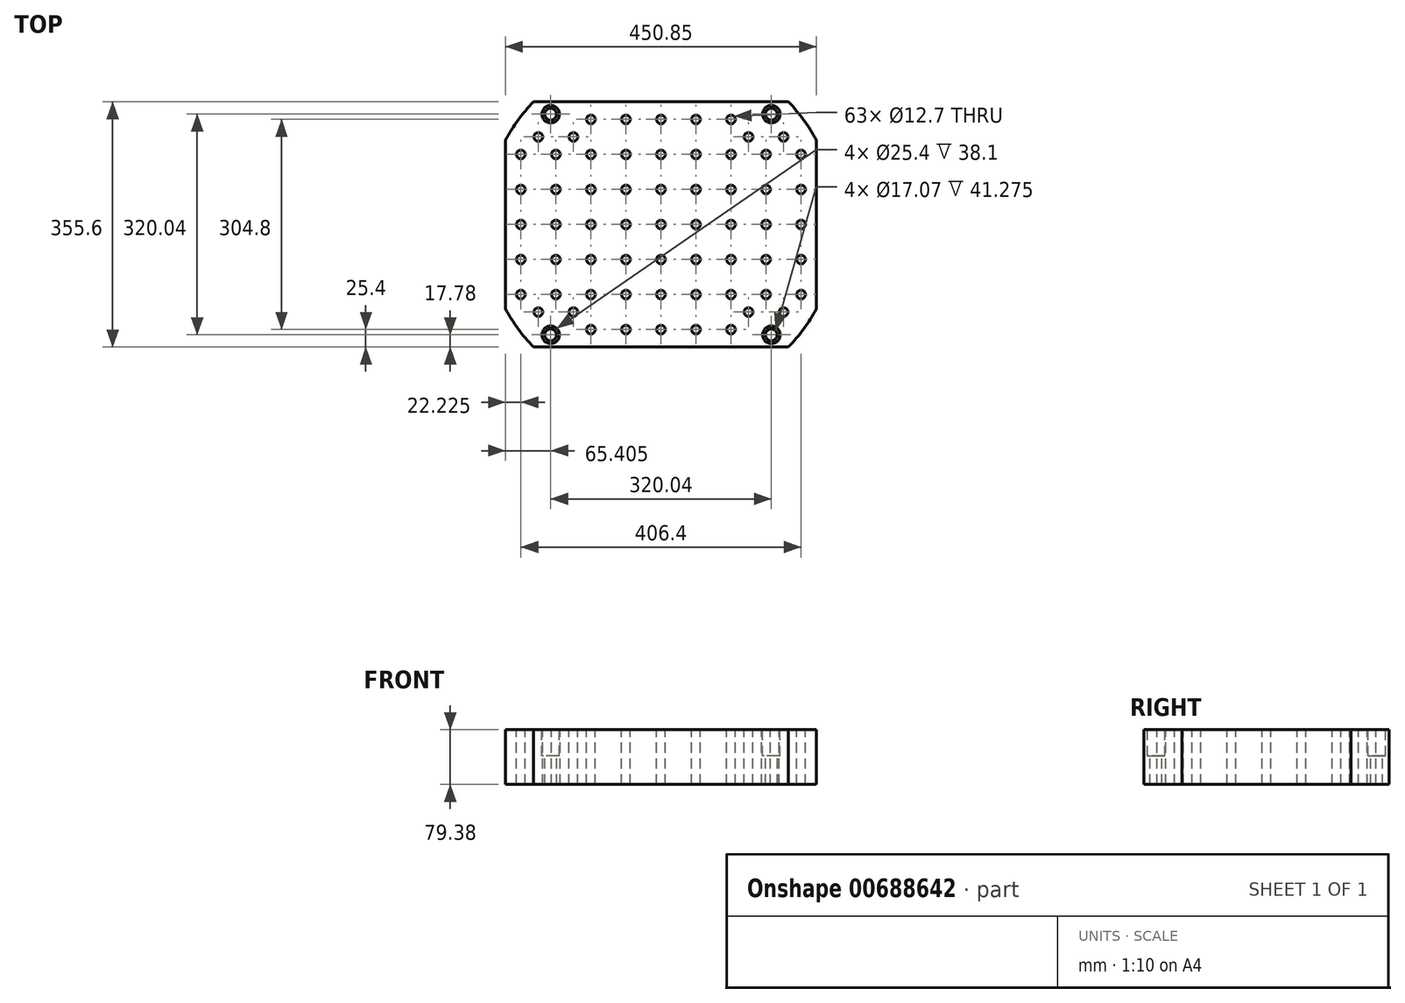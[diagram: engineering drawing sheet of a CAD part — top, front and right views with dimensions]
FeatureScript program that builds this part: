
annotation { "Feature Type Name" : "Feature", "Feature Type Description" : "" }
export const myFeature = defineFeature(function(context is Context, id is Id, definition is map)
    precondition{}
    {
        {
            var Q0;
            Q0=qCreatedBy(makeId("Top.planeOp"),FACE);
            var sketch = newSketch(context, id + "F0", { "sketchPlane" : qUnion([Q0])});
            skLineSegment(sketch, "E0.bottom", {"start": v(0, 0) * mm, "end": v(-450.85, 0) * mm});
            skLineSegment(sketch, "E0.top", {"start": v(0, -355.6) * mm, "end": v(-450.85, -355.6) * mm});
            skLineSegment(sketch, "E0.left", {"start": v(0, 0) * mm, "end": v(0, -355.6) * mm});
            skLineSegment(sketch, "E0.right", {"start": v(-450.85, 0) * mm, "end": v(-450.85, -355.6) * mm});
            skSolve(sketch);
        }
        {
            var Q0;
            Q0=makeQuery(id+"F0.imprint","IMPRINT",FACE,{"disambiguationData":[TD([[makeQuery(id+"F0.imprint","IMPRINT",EDGE,{"derivedFrom":sQuery(id+"F0.wireOp",EDGE,"E0.bottom")}),1.0]])]});
            extrude(context, id + "F1", {"entities" : qUnion([Q0]), "oppositeDirection" : true, "depth" : 79.38 * mm, "offsetDistance" : 25.4 * mm});
        }
        {
            var Q0;
            Q0=makeQuery(id+"F1.opExtrude","CAP_FACE",FACE,{"disambiguationData":[OSD([sQuery(id+"F0.wireOp",EDGE,"E0.bottom"),sQuery(id+"F0.wireOp",EDGE,"E0.top"),sQuery(id+"F0.wireOp",EDGE,"E0.left"),sQuery(id+"F0.wireOp",EDGE,"E0.right")])],"isStart":true});
            var sketch = newSketch(context, id + "F2", { "sketchPlane" : qUnion([Q0])});
            skCircle(sketch, "E1", {"center": v(-225.42, -177.8) * mm, "radius": 256.54 * mm});
            skLineSegment(sketch, "E2", {"start": v(-450.85, 0) * mm, "end": v(0, -355.6) * mm, "construction": true});
            skLineSegment(sketch, "E3", {"start": v(-450.85, -355.6) * mm, "end": v(0, 0) * mm, "construction": true});
            skSolve(sketch);
        }
        {
            var Q0;
            {var subQ0=sQuery(id+"F2.wireOp",EDGE,"E1");var subQ1=makeQuery(id+"F1.opExtrude","CAP_EDGE",EDGE,{"disambiguationData":[OSD([sQuery(id+"F0.wireOp",EDGE,"E0.bottom")])],"isStart":true});var subQ2=makeQuery(id+"F2.imprint","INTERSECT",VERTEX,{"disambiguationData":[OD(1.0)],"derivedFrom":[subQ1,subQ0]});Q0=makeQuery(id+"F2.imprint","IMPRINT",FACE,{"disambiguationData":[TD([[makeQuery(id+"F2.imprint","IMPRINT",EDGE,{"disambiguationData":[TD([[subQ2,-1.0]])],"derivedFrom":subQ0}),-1.0]])]});}
            var Q1;
            {var subQ0=sQuery(id+"F2.wireOp",EDGE,"E1");var subQ1=makeQuery(id+"F1.opExtrude","CAP_EDGE",EDGE,{"disambiguationData":[OSD([sQuery(id+"F0.wireOp",EDGE,"E0.bottom")])],"isStart":true});var subQ2=makeQuery(id+"F2.imprint","INTERSECT",VERTEX,{"disambiguationData":[OD(0.0)],"derivedFrom":[subQ1,subQ0]});Q1=makeQuery(id+"F2.imprint","IMPRINT",FACE,{"disambiguationData":[TD([[makeQuery(id+"F2.imprint","IMPRINT",EDGE,{"disambiguationData":[TD([[subQ2,1.0]])],"derivedFrom":subQ0}),-1.0]])]});}
            var Q2;
            {var subQ0=sQuery(id+"F2.wireOp",EDGE,"E1");var subQ1=makeQuery(id+"F1.opExtrude","CAP_EDGE",EDGE,{"disambiguationData":[OSD([sQuery(id+"F0.wireOp",EDGE,"E0.top")])],"isStart":true});var subQ2=makeQuery(id+"F2.imprint","INTERSECT",VERTEX,{"disambiguationData":[OD(1.0)],"derivedFrom":[subQ1,subQ0]});Q2=makeQuery(id+"F2.imprint","IMPRINT",FACE,{"disambiguationData":[TD([[makeQuery(id+"F2.imprint","IMPRINT",EDGE,{"disambiguationData":[TD([[subQ2,-1.0]])],"derivedFrom":subQ0}),-1.0]])]});}
            var Q3;
            {var subQ0=sQuery(id+"F2.wireOp",EDGE,"E1");var subQ1=makeQuery(id+"F1.opExtrude","CAP_EDGE",EDGE,{"disambiguationData":[OSD([sQuery(id+"F0.wireOp",EDGE,"E0.right")])],"isStart":true});var subQ2=makeQuery(id+"F2.imprint","INTERSECT",VERTEX,{"disambiguationData":[OD(1.0)],"derivedFrom":[subQ1,subQ0]});Q3=makeQuery(id+"F2.imprint","IMPRINT",FACE,{"disambiguationData":[TD([[makeQuery(id+"F2.imprint","IMPRINT",EDGE,{"disambiguationData":[TD([[subQ2,-1.0]])],"derivedFrom":subQ0}),-1.0]])]});}
            extrude(context, id + "F3", {"entities" : qUnion([Q0, Q1, Q2, Q3]), "operationType" : NewBodyOperationType.REMOVE, "endBound" : BoundingType.THROUGH_ALL, "oppositeDirection" : true, "depth" : 25.4 * mm, "offsetDistance" : 25.4 * mm});
        }
        {
            var Q0;
            Q0=makeQuery(id+"F1.opExtrude","CAP_FACE",FACE,{"disambiguationData":[OSD([sQuery(id+"F0.wireOp",EDGE,"E0.bottom"),sQuery(id+"F0.wireOp",EDGE,"E0.top"),sQuery(id+"F0.wireOp",EDGE,"E0.left"),sQuery(id+"F0.wireOp",EDGE,"E0.right")])],"isStart":true});
            var sketch = newSketch(context, id + "F4", { "sketchPlane" : qUnion([Q0])});
            skLineSegment(sketch, "E4", {"start": v(-450.85, -177.8) * mm, "end": v(0, -177.8) * mm, "construction": true});
            skLineSegment(sketch, "E5", {"start": v(-225.42, 0) * mm, "end": v(-225.42, -355.6) * mm, "construction": true});
            skCircle(sketch, "E6", {"center": v(-385.44, -337.82) * mm, "radius": 12.7 * mm});
            skCircle(sketch, "E7", {"center": v(-65.4, -17.78) * mm, "radius": 12.7 * mm});
            skCircle(sketch, "E8", {"center": v(-65.4, -337.82) * mm, "radius": 12.7 * mm});
            skCircle(sketch, "E9", {"center": v(-385.44, -17.78) * mm, "radius": 12.7 * mm});
            skCircle(sketch, "E10", {"center": v(-385.44, -337.82) * mm, "radius": 8.53 * mm});
            skCircle(sketch, "E11", {"center": v(-65.4, -337.82) * mm, "radius": 8.53 * mm});
            skCircle(sketch, "E12", {"center": v(-65.4, -17.78) * mm, "radius": 8.53 * mm});
            skCircle(sketch, "E13", {"center": v(-385.44, -17.78) * mm, "radius": 8.53 * mm});
            skSolve(sketch);
        }
        {
            var Q0;
            Q0 = qSketchRegion(id + "F4", true);
            extrude(context, id + "F5", {"entities" : qUnion([Q0]), "operationType" : NewBodyOperationType.REMOVE, "oppositeDirection" : true, "depth" : 38.1 * mm, "offsetDistance" : 25.4 * mm});
        }
        {
            var Q0;
            Q0=makeQuery(id+"F4.imprint","IMPRINT",FACE,{"disambiguationData":[TD([[makeQuery(id+"F4.imprint","IMPRINT",EDGE,{"derivedFrom":sQuery(id+"F4.wireOp",EDGE,"E10")}),1.0]])]});
            var Q1;
            Q1=makeQuery(id+"F4.imprint","IMPRINT",FACE,{"disambiguationData":[TD([[makeQuery(id+"F4.imprint","IMPRINT",EDGE,{"derivedFrom":sQuery(id+"F4.wireOp",EDGE,"E11")}),1.0]])]});
            var Q2;
            Q2=makeQuery(id+"F4.imprint","IMPRINT",FACE,{"disambiguationData":[TD([[makeQuery(id+"F4.imprint","IMPRINT",EDGE,{"derivedFrom":sQuery(id+"F4.wireOp",EDGE,"E12")}),1.0]])]});
            var Q3;
            Q3=makeQuery(id+"F4.imprint","IMPRINT",FACE,{"disambiguationData":[TD([[makeQuery(id+"F4.imprint","IMPRINT",EDGE,{"derivedFrom":sQuery(id+"F4.wireOp",EDGE,"E13")}),1.0]])]});
            extrude(context, id + "F6", {"entities" : qUnion([Q0, Q1, Q2, Q3]), "operationType" : NewBodyOperationType.REMOVE, "endBound" : BoundingType.THROUGH_ALL, "oppositeDirection" : true, "depth" : 25.4 * mm, "offsetDistance" : 25.4 * mm});
        }
        {
            var Q0;
            Q0=makeQuery(id+"F4.imprint","IMPRINT",FACE,{"disambiguationData":[TD([[makeQuery(id+"F4.imprint","IMPRINT",EDGE,{"derivedFrom":sQuery(id+"F4.wireOp",EDGE,"E6")}),-1.0]])]});
            var sketch = newSketch(context, id + "F7", { "sketchPlane" : qUnion([Q0])});
            skCircle(sketch, "E14", {"center": v(-428.62, -330.2) * mm, "radius": 6.35 * mm});
            skCircle(sketch, "E15.0.1.0", {"center": v(-428.62, -279.4) * mm, "radius": 6.35 * mm});
            skCircle(sketch, "E15.0.2.0", {"center": v(-428.62, -228.6) * mm, "radius": 6.35 * mm});
            skCircle(sketch, "E15.0.3.0", {"center": v(-428.62, -177.8) * mm, "radius": 6.35 * mm});
            skCircle(sketch, "E15.0.4.0", {"center": v(-428.62, -127) * mm, "radius": 6.35 * mm});
            skCircle(sketch, "E15.0.5.0", {"center": v(-428.62, -76.2) * mm, "radius": 6.35 * mm});
            skCircle(sketch, "E15.0.6.0", {"center": v(-428.62, -25.4) * mm, "radius": 6.35 * mm});
            skCircle(sketch, "E15.1.0.0", {"center": v(-377.82, -330.2) * mm, "radius": 6.35 * mm});
            skCircle(sketch, "E15.1.1.0", {"center": v(-377.82, -279.4) * mm, "radius": 6.35 * mm});
            skCircle(sketch, "E15.1.2.0", {"center": v(-377.82, -228.6) * mm, "radius": 6.35 * mm});
            skCircle(sketch, "E15.1.3.0", {"center": v(-377.82, -177.8) * mm, "radius": 6.35 * mm});
            skCircle(sketch, "E15.1.4.0", {"center": v(-377.82, -127) * mm, "radius": 6.35 * mm});
            skCircle(sketch, "E15.1.5.0", {"center": v(-377.82, -76.2) * mm, "radius": 6.35 * mm});
            skCircle(sketch, "E15.1.6.0", {"center": v(-377.82, -25.4) * mm, "radius": 6.35 * mm});
            skCircle(sketch, "E15.2.0.0", {"center": v(-327.02, -330.2) * mm, "radius": 6.35 * mm});
            skCircle(sketch, "E15.2.1.0", {"center": v(-327.02, -279.4) * mm, "radius": 6.35 * mm});
            skCircle(sketch, "E15.2.2.0", {"center": v(-327.02, -228.6) * mm, "radius": 6.35 * mm});
            skCircle(sketch, "E15.2.3.0", {"center": v(-327.02, -177.8) * mm, "radius": 6.35 * mm});
            skCircle(sketch, "E15.2.4.0", {"center": v(-327.02, -127) * mm, "radius": 6.35 * mm});
            skCircle(sketch, "E15.2.5.0", {"center": v(-327.02, -76.2) * mm, "radius": 6.35 * mm});
            skCircle(sketch, "E15.2.6.0", {"center": v(-327.02, -25.4) * mm, "radius": 6.35 * mm});
            skCircle(sketch, "E15.3.0.0", {"center": v(-276.22, -330.2) * mm, "radius": 6.35 * mm});
            skCircle(sketch, "E15.3.1.0", {"center": v(-276.22, -279.4) * mm, "radius": 6.35 * mm});
            skCircle(sketch, "E15.3.2.0", {"center": v(-276.22, -228.6) * mm, "radius": 6.35 * mm});
            skCircle(sketch, "E15.3.3.0", {"center": v(-276.22, -177.8) * mm, "radius": 6.35 * mm});
            skCircle(sketch, "E15.3.4.0", {"center": v(-276.22, -127) * mm, "radius": 6.35 * mm});
            skCircle(sketch, "E15.3.5.0", {"center": v(-276.22, -76.2) * mm, "radius": 6.35 * mm});
            skCircle(sketch, "E15.3.6.0", {"center": v(-276.22, -25.4) * mm, "radius": 6.35 * mm});
            skCircle(sketch, "E15.4.0.0", {"center": v(-225.42, -330.2) * mm, "radius": 6.35 * mm});
            skCircle(sketch, "E15.4.1.0", {"center": v(-225.42, -279.4) * mm, "radius": 6.35 * mm});
            skCircle(sketch, "E15.4.2.0", {"center": v(-225.42, -228.6) * mm, "radius": 6.35 * mm});
            skCircle(sketch, "E15.4.3.0", {"center": v(-225.42, -177.8) * mm, "radius": 6.35 * mm});
            skCircle(sketch, "E15.4.4.0", {"center": v(-225.42, -127) * mm, "radius": 6.35 * mm});
            skCircle(sketch, "E15.4.5.0", {"center": v(-225.42, -76.2) * mm, "radius": 6.35 * mm});
            skCircle(sketch, "E15.4.6.0", {"center": v(-225.42, -25.4) * mm, "radius": 6.35 * mm});
            skCircle(sketch, "E15.5.0.0", {"center": v(-174.62, -330.2) * mm, "radius": 6.35 * mm});
            skCircle(sketch, "E15.5.1.0", {"center": v(-174.62, -279.4) * mm, "radius": 6.35 * mm});
            skCircle(sketch, "E15.5.2.0", {"center": v(-174.62, -228.6) * mm, "radius": 6.35 * mm});
            skCircle(sketch, "E15.5.3.0", {"center": v(-174.62, -177.8) * mm, "radius": 6.35 * mm});
            skCircle(sketch, "E15.5.4.0", {"center": v(-174.62, -127) * mm, "radius": 6.35 * mm});
            skCircle(sketch, "E15.5.5.0", {"center": v(-174.62, -76.2) * mm, "radius": 6.35 * mm});
            skCircle(sketch, "E15.5.6.0", {"center": v(-174.62, -25.4) * mm, "radius": 6.35 * mm});
            skCircle(sketch, "E15.6.0.0", {"center": v(-123.82, -330.2) * mm, "radius": 6.35 * mm});
            skCircle(sketch, "E15.6.1.0", {"center": v(-123.82, -279.4) * mm, "radius": 6.35 * mm});
            skCircle(sketch, "E15.6.2.0", {"center": v(-123.82, -228.6) * mm, "radius": 6.35 * mm});
            skCircle(sketch, "E15.6.3.0", {"center": v(-123.82, -177.8) * mm, "radius": 6.35 * mm});
            skCircle(sketch, "E15.6.4.0", {"center": v(-123.82, -127) * mm, "radius": 6.35 * mm});
            skCircle(sketch, "E15.6.5.0", {"center": v(-123.82, -76.2) * mm, "radius": 6.35 * mm});
            skCircle(sketch, "E15.6.6.0", {"center": v(-123.82, -25.4) * mm, "radius": 6.35 * mm});
            skCircle(sketch, "E15.7.0.0", {"center": v(-73.02, -330.2) * mm, "radius": 6.35 * mm});
            skCircle(sketch, "E15.7.1.0", {"center": v(-73.02, -279.4) * mm, "radius": 6.35 * mm});
            skCircle(sketch, "E15.7.2.0", {"center": v(-73.02, -228.6) * mm, "radius": 6.35 * mm});
            skCircle(sketch, "E15.7.3.0", {"center": v(-73.02, -177.8) * mm, "radius": 6.35 * mm});
            skCircle(sketch, "E15.7.4.0", {"center": v(-73.02, -127) * mm, "radius": 6.35 * mm});
            skCircle(sketch, "E15.7.5.0", {"center": v(-73.02, -76.2) * mm, "radius": 6.35 * mm});
            skCircle(sketch, "E15.7.6.0", {"center": v(-73.02, -25.4) * mm, "radius": 6.35 * mm});
            skLineSegment(sketch, "E15.direction1", {"start": v(-428.62, -330.2) * mm, "end": v(-377.82, -330.2) * mm, "construction": true});
            skLineSegment(sketch, "E15.direction2", {"start": v(-428.62, -330.2) * mm, "end": v(-428.62, -279.4) * mm, "construction": true});
            skCircle(sketch, "E16.0.8.0", {"center": v(-22.22, -330.2) * mm, "radius": 6.35 * mm});
            skCircle(sketch, "E16.0.8.1", {"center": v(-22.22, -279.4) * mm, "radius": 6.35 * mm});
            skCircle(sketch, "E16.0.8.2", {"center": v(-22.22, -228.6) * mm, "radius": 6.35 * mm});
            skCircle(sketch, "E16.0.8.3", {"center": v(-22.22, -177.8) * mm, "radius": 6.35 * mm});
            skCircle(sketch, "E16.0.8.4", {"center": v(-22.22, -127) * mm, "radius": 6.35 * mm});
            skCircle(sketch, "E16.0.8.5", {"center": v(-22.22, -76.2) * mm, "radius": 6.35 * mm});
            skCircle(sketch, "E16.0.8.6", {"center": v(-22.22, -25.4) * mm, "radius": 6.35 * mm});
            skSolve(sketch);
        }
        {
            var Q0;
            Q0=makeQuery(id+"F7.imprint","IMPRINT",FACE,{"disambiguationData":[TD([[makeQuery(id+"F7.imprint","IMPRINT",EDGE,{"derivedFrom":sQuery(id+"F7.wireOp",EDGE,"E15.1.5.0")}),1.0]])]});
            var Q1;
            Q1=makeQuery(id+"F7.imprint","IMPRINT",FACE,{"disambiguationData":[TD([[makeQuery(id+"F7.imprint","IMPRINT",EDGE,{"derivedFrom":sQuery(id+"F7.wireOp",EDGE,"E15.0.5.0")}),1.0]])]});
            var Q2;
            Q2=makeQuery(id+"F7.imprint","IMPRINT",FACE,{"disambiguationData":[TD([[makeQuery(id+"F7.imprint","IMPRINT",EDGE,{"derivedFrom":sQuery(id+"F7.wireOp",EDGE,"E15.2.6.0")}),1.0]])]});
            var Q3;
            Q3=makeQuery(id+"F7.imprint","IMPRINT",FACE,{"disambiguationData":[TD([[makeQuery(id+"F7.imprint","IMPRINT",EDGE,{"derivedFrom":sQuery(id+"F7.wireOp",EDGE,"E15.3.6.0")}),1.0]])]});
            var Q4;
            Q4=makeQuery(id+"F7.imprint","IMPRINT",FACE,{"disambiguationData":[TD([[makeQuery(id+"F7.imprint","IMPRINT",EDGE,{"derivedFrom":sQuery(id+"F7.wireOp",EDGE,"E15.4.6.0")}),1.0]])]});
            var Q5;
            Q5=makeQuery(id+"F7.imprint","IMPRINT",FACE,{"disambiguationData":[TD([[makeQuery(id+"F7.imprint","IMPRINT",EDGE,{"derivedFrom":sQuery(id+"F7.wireOp",EDGE,"E15.5.6.0")}),1.0]])]});
            var Q6;
            Q6=makeQuery(id+"F7.imprint","IMPRINT",FACE,{"disambiguationData":[TD([[makeQuery(id+"F7.imprint","IMPRINT",EDGE,{"derivedFrom":sQuery(id+"F7.wireOp",EDGE,"E15.6.6.0")}),1.0]])]});
            var Q7;
            Q7=makeQuery(id+"F7.imprint","IMPRINT",FACE,{"disambiguationData":[TD([[makeQuery(id+"F7.imprint","IMPRINT",EDGE,{"derivedFrom":sQuery(id+"F7.wireOp",EDGE,"E15.7.5.0")}),1.0]])]});
            var Q8;
            Q8=makeQuery(id+"F7.imprint","IMPRINT",FACE,{"disambiguationData":[TD([[makeQuery(id+"F7.imprint","IMPRINT",EDGE,{"derivedFrom":sQuery(id+"F7.wireOp",EDGE,"E15.6.4.0")}),1.0]])]});
            var Q9;
            Q9=makeQuery(id+"F7.imprint","IMPRINT",FACE,{"disambiguationData":[TD([[makeQuery(id+"F7.imprint","IMPRINT",EDGE,{"derivedFrom":sQuery(id+"F7.wireOp",EDGE,"E15.7.4.0")}),1.0]])]});
            var Q10;
            Q10=makeQuery(id+"F7.imprint","IMPRINT",FACE,{"disambiguationData":[TD([[makeQuery(id+"F7.imprint","IMPRINT",EDGE,{"derivedFrom":sQuery(id+"F7.wireOp",EDGE,"E16.0.8.4")}),1.0]])]});
            var Q11;
            Q11=makeQuery(id+"F7.imprint","IMPRINT",FACE,{"disambiguationData":[TD([[makeQuery(id+"F7.imprint","IMPRINT",EDGE,{"derivedFrom":sQuery(id+"F7.wireOp",EDGE,"E16.0.8.5")}),1.0]])]});
            var Q12;
            Q12=makeQuery(id+"F7.imprint","IMPRINT",FACE,{"disambiguationData":[TD([[makeQuery(id+"F7.imprint","IMPRINT",EDGE,{"derivedFrom":sQuery(id+"F7.wireOp",EDGE,"E15.6.5.0")}),1.0]])]});
            var Q13;
            Q13=makeQuery(id+"F7.imprint","IMPRINT",FACE,{"disambiguationData":[TD([[makeQuery(id+"F7.imprint","IMPRINT",EDGE,{"derivedFrom":sQuery(id+"F7.wireOp",EDGE,"E15.5.5.0")}),1.0]])]});
            var Q14;
            Q14=makeQuery(id+"F7.imprint","IMPRINT",FACE,{"disambiguationData":[TD([[makeQuery(id+"F7.imprint","IMPRINT",EDGE,{"derivedFrom":sQuery(id+"F7.wireOp",EDGE,"E15.4.5.0")}),1.0]])]});
            var Q15;
            Q15=makeQuery(id+"F7.imprint","IMPRINT",FACE,{"disambiguationData":[TD([[makeQuery(id+"F7.imprint","IMPRINT",EDGE,{"derivedFrom":sQuery(id+"F7.wireOp",EDGE,"E15.3.5.0")}),1.0]])]});
            var Q16;
            Q16=makeQuery(id+"F7.imprint","IMPRINT",FACE,{"disambiguationData":[TD([[makeQuery(id+"F7.imprint","IMPRINT",EDGE,{"derivedFrom":sQuery(id+"F7.wireOp",EDGE,"E15.2.5.0")}),1.0]])]});
            var Q17;
            Q17=makeQuery(id+"F7.imprint","IMPRINT",FACE,{"disambiguationData":[TD([[makeQuery(id+"F7.imprint","IMPRINT",EDGE,{"derivedFrom":sQuery(id+"F7.wireOp",EDGE,"E15.0.4.0")}),1.0]])]});
            var Q18;
            Q18=makeQuery(id+"F7.imprint","IMPRINT",FACE,{"disambiguationData":[TD([[makeQuery(id+"F7.imprint","IMPRINT",EDGE,{"derivedFrom":sQuery(id+"F7.wireOp",EDGE,"E15.2.4.0")}),1.0]])]});
            var Q19;
            Q19=makeQuery(id+"F7.imprint","IMPRINT",FACE,{"disambiguationData":[TD([[makeQuery(id+"F7.imprint","IMPRINT",EDGE,{"derivedFrom":sQuery(id+"F7.wireOp",EDGE,"E15.3.4.0")}),1.0]])]});
            var Q20;
            Q20=makeQuery(id+"F7.imprint","IMPRINT",FACE,{"disambiguationData":[TD([[makeQuery(id+"F7.imprint","IMPRINT",EDGE,{"derivedFrom":sQuery(id+"F7.wireOp",EDGE,"E15.4.4.0")}),1.0]])]});
            var Q21;
            Q21=makeQuery(id+"F7.imprint","IMPRINT",FACE,{"disambiguationData":[TD([[makeQuery(id+"F7.imprint","IMPRINT",EDGE,{"derivedFrom":sQuery(id+"F7.wireOp",EDGE,"E15.5.4.0")}),1.0]])]});
            var Q22;
            Q22=makeQuery(id+"F7.imprint","IMPRINT",FACE,{"disambiguationData":[TD([[makeQuery(id+"F7.imprint","IMPRINT",EDGE,{"derivedFrom":sQuery(id+"F7.wireOp",EDGE,"E15.4.3.0")}),1.0]])]});
            var Q23;
            Q23=makeQuery(id+"F7.imprint","IMPRINT",FACE,{"disambiguationData":[TD([[makeQuery(id+"F7.imprint","IMPRINT",EDGE,{"derivedFrom":sQuery(id+"F7.wireOp",EDGE,"E15.3.3.0")}),1.0]])]});
            var Q24;
            Q24=makeQuery(id+"F7.imprint","IMPRINT",FACE,{"disambiguationData":[TD([[makeQuery(id+"F7.imprint","IMPRINT",EDGE,{"derivedFrom":sQuery(id+"F7.wireOp",EDGE,"E15.2.3.0")}),1.0]])]});
            var Q25;
            Q25=makeQuery(id+"F7.imprint","IMPRINT",FACE,{"disambiguationData":[TD([[makeQuery(id+"F7.imprint","IMPRINT",EDGE,{"derivedFrom":sQuery(id+"F7.wireOp",EDGE,"E15.1.3.0")}),1.0]])]});
            var Q26;
            Q26=makeQuery(id+"F7.imprint","IMPRINT",FACE,{"disambiguationData":[TD([[makeQuery(id+"F7.imprint","IMPRINT",EDGE,{"derivedFrom":sQuery(id+"F7.wireOp",EDGE,"E15.0.3.0")}),1.0]])]});
            var Q27;
            Q27=makeQuery(id+"F7.imprint","IMPRINT",FACE,{"disambiguationData":[TD([[makeQuery(id+"F7.imprint","IMPRINT",EDGE,{"derivedFrom":sQuery(id+"F7.wireOp",EDGE,"E15.5.3.0")}),1.0]])]});
            var Q28;
            Q28=makeQuery(id+"F7.imprint","IMPRINT",FACE,{"disambiguationData":[TD([[makeQuery(id+"F7.imprint","IMPRINT",EDGE,{"derivedFrom":sQuery(id+"F7.wireOp",EDGE,"E15.7.3.0")}),1.0]])]});
            var Q29;
            Q29=makeQuery(id+"F7.imprint","IMPRINT",FACE,{"disambiguationData":[TD([[makeQuery(id+"F7.imprint","IMPRINT",EDGE,{"derivedFrom":sQuery(id+"F7.wireOp",EDGE,"E15.6.3.0")}),1.0]])]});
            var Q30;
            Q30=makeQuery(id+"F7.imprint","IMPRINT",FACE,{"disambiguationData":[TD([[makeQuery(id+"F7.imprint","IMPRINT",EDGE,{"derivedFrom":sQuery(id+"F7.wireOp",EDGE,"E16.0.8.3")}),1.0]])]});
            var Q31;
            Q31=makeQuery(id+"F7.imprint","IMPRINT",FACE,{"disambiguationData":[TD([[makeQuery(id+"F7.imprint","IMPRINT",EDGE,{"derivedFrom":sQuery(id+"F7.wireOp",EDGE,"E16.0.8.2")}),1.0]])]});
            var Q32;
            Q32=makeQuery(id+"F7.imprint","IMPRINT",FACE,{"disambiguationData":[TD([[makeQuery(id+"F7.imprint","IMPRINT",EDGE,{"derivedFrom":sQuery(id+"F7.wireOp",EDGE,"E15.6.2.0")}),1.0]])]});
            var Q33;
            Q33=makeQuery(id+"F7.imprint","IMPRINT",FACE,{"disambiguationData":[TD([[makeQuery(id+"F7.imprint","IMPRINT",EDGE,{"derivedFrom":sQuery(id+"F7.wireOp",EDGE,"E15.5.2.0")}),1.0]])]});
            var Q34;
            Q34=makeQuery(id+"F7.imprint","IMPRINT",FACE,{"disambiguationData":[TD([[makeQuery(id+"F7.imprint","IMPRINT",EDGE,{"derivedFrom":sQuery(id+"F7.wireOp",EDGE,"E15.7.2.0")}),1.0]])]});
            var Q35;
            Q35=makeQuery(id+"F7.imprint","IMPRINT",FACE,{"disambiguationData":[TD([[makeQuery(id+"F7.imprint","IMPRINT",EDGE,{"derivedFrom":sQuery(id+"F7.wireOp",EDGE,"E15.4.2.0")}),1.0]])]});
            var Q36;
            Q36=makeQuery(id+"F7.imprint","IMPRINT",FACE,{"disambiguationData":[TD([[makeQuery(id+"F7.imprint","IMPRINT",EDGE,{"derivedFrom":sQuery(id+"F7.wireOp",EDGE,"E15.3.2.0")}),1.0]])]});
            var Q37;
            Q37=makeQuery(id+"F7.imprint","IMPRINT",FACE,{"disambiguationData":[TD([[makeQuery(id+"F7.imprint","IMPRINT",EDGE,{"derivedFrom":sQuery(id+"F7.wireOp",EDGE,"E15.2.2.0")}),1.0]])]});
            var Q38;
            Q38=makeQuery(id+"F7.imprint","IMPRINT",FACE,{"disambiguationData":[TD([[makeQuery(id+"F7.imprint","IMPRINT",EDGE,{"derivedFrom":sQuery(id+"F7.wireOp",EDGE,"E15.1.4.0")}),1.0]])]});
            var Q39;
            Q39=makeQuery(id+"F7.imprint","IMPRINT",FACE,{"disambiguationData":[TD([[makeQuery(id+"F7.imprint","IMPRINT",EDGE,{"derivedFrom":sQuery(id+"F7.wireOp",EDGE,"E15.1.2.0")}),1.0]])]});
            var Q40;
            Q40=makeQuery(id+"F7.imprint","IMPRINT",FACE,{"disambiguationData":[TD([[makeQuery(id+"F7.imprint","IMPRINT",EDGE,{"derivedFrom":sQuery(id+"F7.wireOp",EDGE,"E15.0.2.0")}),1.0]])]});
            var Q41;
            Q41=makeQuery(id+"F7.imprint","IMPRINT",FACE,{"disambiguationData":[TD([[makeQuery(id+"F7.imprint","IMPRINT",EDGE,{"derivedFrom":sQuery(id+"F7.wireOp",EDGE,"E15.2.1.0")}),1.0]])]});
            var Q42;
            Q42=makeQuery(id+"F7.imprint","IMPRINT",FACE,{"disambiguationData":[TD([[makeQuery(id+"F7.imprint","IMPRINT",EDGE,{"derivedFrom":sQuery(id+"F7.wireOp",EDGE,"E15.1.1.0")}),1.0]])]});
            var Q43;
            Q43=makeQuery(id+"F7.imprint","IMPRINT",FACE,{"disambiguationData":[TD([[makeQuery(id+"F7.imprint","IMPRINT",EDGE,{"derivedFrom":sQuery(id+"F7.wireOp",EDGE,"E15.0.1.0")}),1.0]])]});
            var Q44;
            Q44=makeQuery(id+"F7.imprint","IMPRINT",FACE,{"disambiguationData":[TD([[makeQuery(id+"F7.imprint","IMPRINT",EDGE,{"derivedFrom":sQuery(id+"F7.wireOp",EDGE,"E15.3.1.0")}),1.0]])]});
            var Q45;
            Q45=makeQuery(id+"F7.imprint","IMPRINT",FACE,{"disambiguationData":[TD([[makeQuery(id+"F7.imprint","IMPRINT",EDGE,{"derivedFrom":sQuery(id+"F7.wireOp",EDGE,"E15.4.1.0")}),1.0]])]});
            var Q46;
            Q46=makeQuery(id+"F7.imprint","IMPRINT",FACE,{"disambiguationData":[TD([[makeQuery(id+"F7.imprint","IMPRINT",EDGE,{"derivedFrom":sQuery(id+"F7.wireOp",EDGE,"E16.0.8.1")}),1.0]])]});
            var Q47;
            Q47=makeQuery(id+"F7.imprint","IMPRINT",FACE,{"disambiguationData":[TD([[makeQuery(id+"F7.imprint","IMPRINT",EDGE,{"derivedFrom":sQuery(id+"F7.wireOp",EDGE,"E15.6.0.0")}),1.0]])]});
            var Q48;
            Q48=makeQuery(id+"F7.imprint","IMPRINT",FACE,{"disambiguationData":[TD([[makeQuery(id+"F7.imprint","IMPRINT",EDGE,{"derivedFrom":sQuery(id+"F7.wireOp",EDGE,"E15.5.0.0")}),1.0]])]});
            var Q49;
            Q49=makeQuery(id+"F7.imprint","IMPRINT",FACE,{"disambiguationData":[TD([[makeQuery(id+"F7.imprint","IMPRINT",EDGE,{"derivedFrom":sQuery(id+"F7.wireOp",EDGE,"E15.4.0.0")}),1.0]])]});
            var Q50;
            Q50=makeQuery(id+"F7.imprint","IMPRINT",FACE,{"disambiguationData":[TD([[makeQuery(id+"F7.imprint","IMPRINT",EDGE,{"derivedFrom":sQuery(id+"F7.wireOp",EDGE,"E15.5.1.0")}),1.0]])]});
            var Q51;
            Q51=makeQuery(id+"F7.imprint","IMPRINT",FACE,{"disambiguationData":[TD([[makeQuery(id+"F7.imprint","IMPRINT",EDGE,{"derivedFrom":sQuery(id+"F7.wireOp",EDGE,"E15.6.1.0")}),1.0]])]});
            var Q52;
            Q52=makeQuery(id+"F7.imprint","IMPRINT",FACE,{"disambiguationData":[TD([[makeQuery(id+"F7.imprint","IMPRINT",EDGE,{"derivedFrom":sQuery(id+"F7.wireOp",EDGE,"E15.7.1.0")}),1.0]])]});
            var Q53;
            Q53=makeQuery(id+"F7.imprint","IMPRINT",FACE,{"disambiguationData":[TD([[makeQuery(id+"F7.imprint","IMPRINT",EDGE,{"derivedFrom":sQuery(id+"F7.wireOp",EDGE,"E15.3.0.0")}),1.0]])]});
            var Q54;
            Q54=makeQuery(id+"F7.imprint","IMPRINT",FACE,{"disambiguationData":[TD([[makeQuery(id+"F7.imprint","IMPRINT",EDGE,{"derivedFrom":sQuery(id+"F7.wireOp",EDGE,"E15.2.0.0")}),1.0]])]});
            extrude(context, id + "F8", {"entities" : qUnion([Q0, Q1, Q2, Q3, Q4, Q5, Q6, Q7, Q8, Q9, Q10, Q11, Q12, Q13, Q14, Q15, Q16, Q17, Q18, Q19, Q20, Q21, Q22, Q23, Q24, Q25, Q26, Q27, Q28, Q29, Q30, Q31, Q32, Q33, Q34, Q35, Q36, Q37, Q38, Q39, Q40, Q41, Q42, Q43, Q44, Q45, Q46, Q47, Q48, Q49, Q50, Q51, Q52, Q53, Q54]), "operationType" : NewBodyOperationType.REMOVE, "endBound" : BoundingType.THROUGH_ALL, "oppositeDirection" : true, "depth" : 25.4 * mm, "offsetDistance" : 25.4 * mm});
        }
        {
            var Q0;
            Q0=makeQuery(id+"F4.imprint","IMPRINT",FACE,{"disambiguationData":[TD([[makeQuery(id+"F4.imprint","IMPRINT",EDGE,{"derivedFrom":sQuery(id+"F4.wireOp",EDGE,"E6")}),-1.0]])]});
            var sketch = newSketch(context, id + "F9", { "sketchPlane" : qUnion([Q0])});
            skCircle(sketch, "E17", {"center": v(-403.22, -304.8) * mm, "radius": 6.35 * mm});
            skCircle(sketch, "E18", {"center": v(-352.42, -304.8) * mm, "radius": 6.35 * mm});
            skCircle(sketch, "E19", {"center": v(-352.42, -50.8) * mm, "radius": 6.35 * mm});
            skCircle(sketch, "E20", {"center": v(-403.22, -50.8) * mm, "radius": 6.35 * mm});
            skCircle(sketch, "E21", {"center": v(-98.42, -50.8) * mm, "radius": 6.35 * mm});
            skCircle(sketch, "E22", {"center": v(-47.62, -50.8) * mm, "radius": 6.35 * mm});
            skCircle(sketch, "E23", {"center": v(-98.42, -304.8) * mm, "radius": 6.35 * mm});
            skCircle(sketch, "E24", {"center": v(-47.62, -304.8) * mm, "radius": 6.35 * mm});
            skSolve(sketch);
        }
        {
            var Q0;
            Q0 = qSketchRegion(id + "F9", true);
            extrude(context, id + "F10", {"entities" : qUnion([Q0]), "operationType" : NewBodyOperationType.REMOVE, "endBound" : BoundingType.THROUGH_ALL, "oppositeDirection" : true, "depth" : 25.4 * mm, "offsetDistance" : 25.4 * mm});
        }
    });
